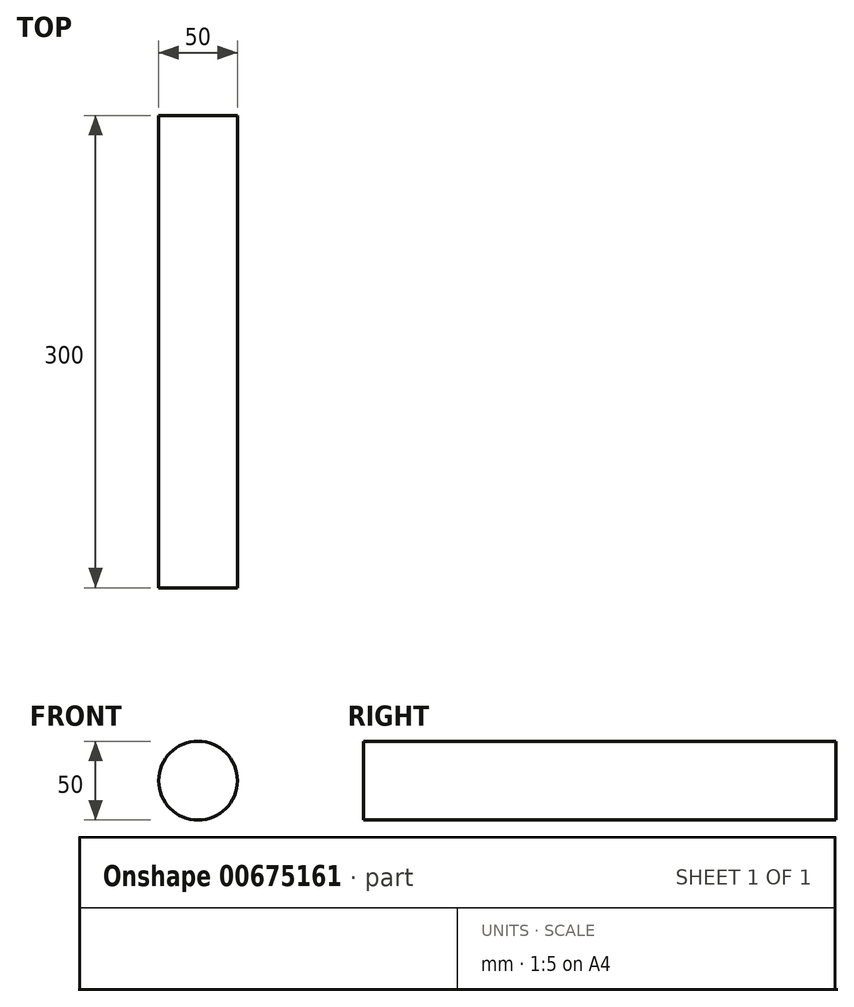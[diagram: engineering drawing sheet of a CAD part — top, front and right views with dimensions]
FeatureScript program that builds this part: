
annotation { "Feature Type Name" : "Feature", "Feature Type Description" : "" }
export const myFeature = defineFeature(function(context is Context, id is Id, definition is map)
    precondition{}
    {
        {
            var Q0;
            Q0=qCreatedBy(makeId("Front.planeOp"),FACE);
            var sketch = newSketch(context, id + "F0", { "sketchPlane" : qUnion([Q0])});
            skCircle(sketch, "E0", {"center": v(0, 0) * mm, "radius": 25 * mm});
            skSolve(sketch);
        }
        {
            var Q0;
            Q0=makeQuery(id+"F0.imprint","IMPRINT",FACE,{"disambiguationData":[TD([[makeQuery(id+"F0.imprint","IMPRINT",EDGE,{"derivedFrom":sQuery(id+"F0.wireOp",EDGE,"E0")}),1.0]])]});
            extrude(context, id + "F1", {"entities" : qUnion([Q0]), "depth" : 300 * mm, "offsetDistance" : 25 * mm});
        }
    });
